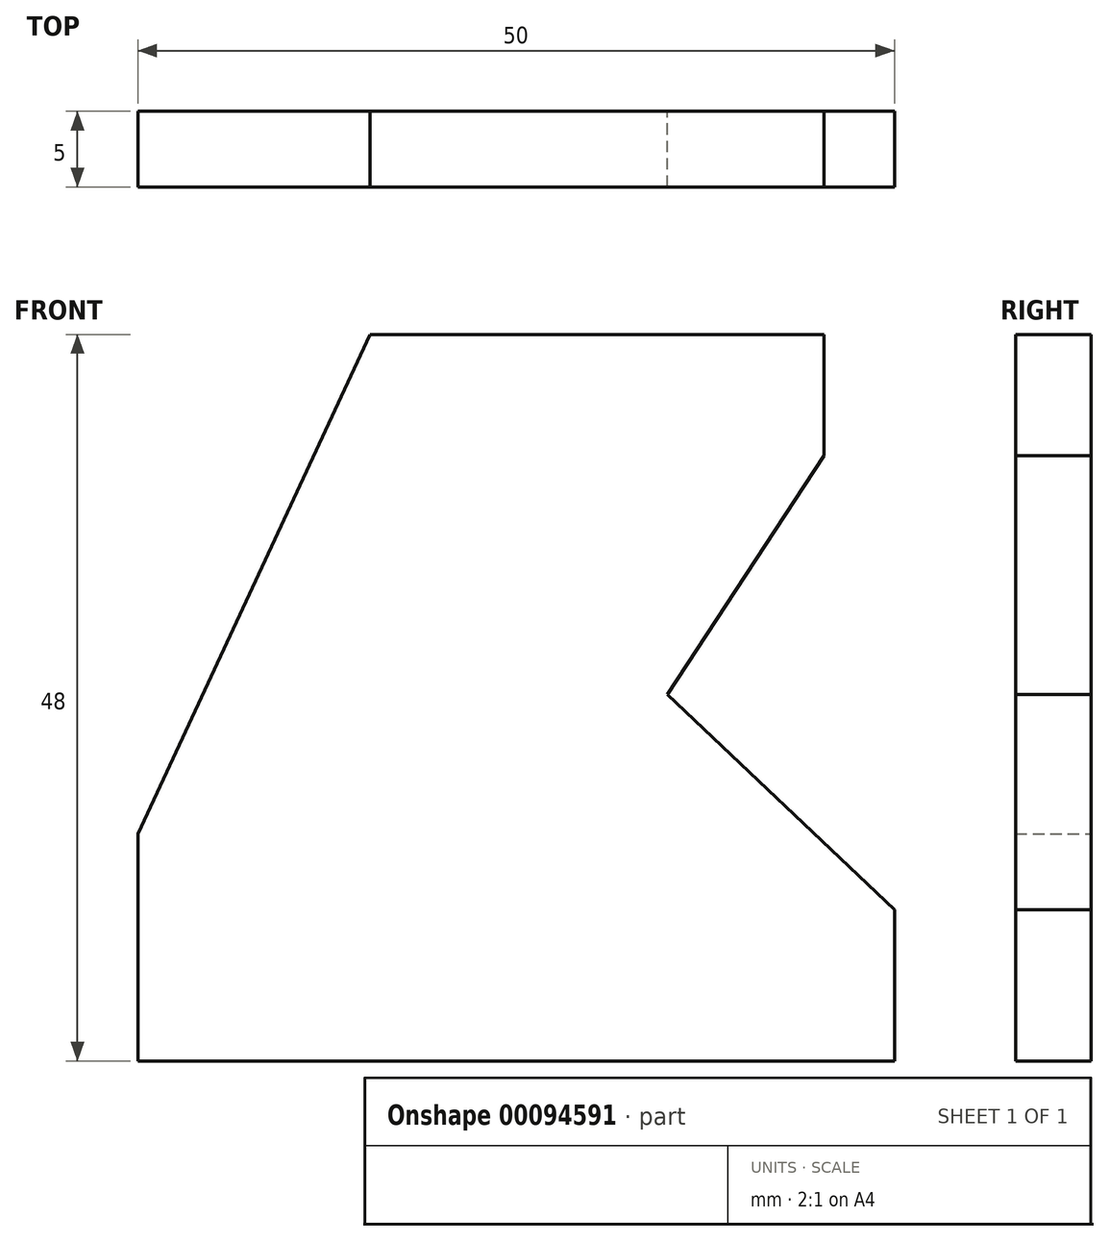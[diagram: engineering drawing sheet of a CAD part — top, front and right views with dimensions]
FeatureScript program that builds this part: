
annotation { "Feature Type Name" : "Feature", "Feature Type Description" : "" }
export const myFeature = defineFeature(function(context is Context, id is Id, definition is map)
    precondition{}
    {
        {
            var Q0;
            Q0=qCreatedBy(makeId("Front.planeOp"),FACE);
            var sketch = newSketch(context, id + "F0", { "sketchPlane" : qUnion([Q0])});
            skLineSegment(sketch, "E0", {"start": v(-30.34, 0) * mm, "end": v(-30.34, -15) * mm});
            skLineSegment(sketch, "E1", {"start": v(-30.34, -15) * mm, "end": v(19.66, -15) * mm});
            skLineSegment(sketch, "E2", {"start": v(19.66, -15) * mm, "end": v(19.66, -5) * mm});
            skLineSegment(sketch, "E3", {"start": v(19.66, -5) * mm, "end": v(4.66, 9.22) * mm});
            skLineSegment(sketch, "E4", {"start": v(4.66, 9.22) * mm, "end": v(15, 25) * mm});
            skLineSegment(sketch, "E5", {"start": v(15, 25) * mm, "end": v(15, 33) * mm});
            skLineSegment(sketch, "E6", {"start": v(15, 33) * mm, "end": v(-15, 33) * mm});
            skLineSegment(sketch, "E7", {"start": v(-15, 33) * mm, "end": v(-30.34, 0) * mm});
            skSolve(sketch);
        }
        {
            var Q0;
            Q0 = qSketchRegion(id + "F0", true);
            extrude(context, id + "F1", {"entities" : qUnion([Q0]), "depth" : 5 * mm});
        }
    });
